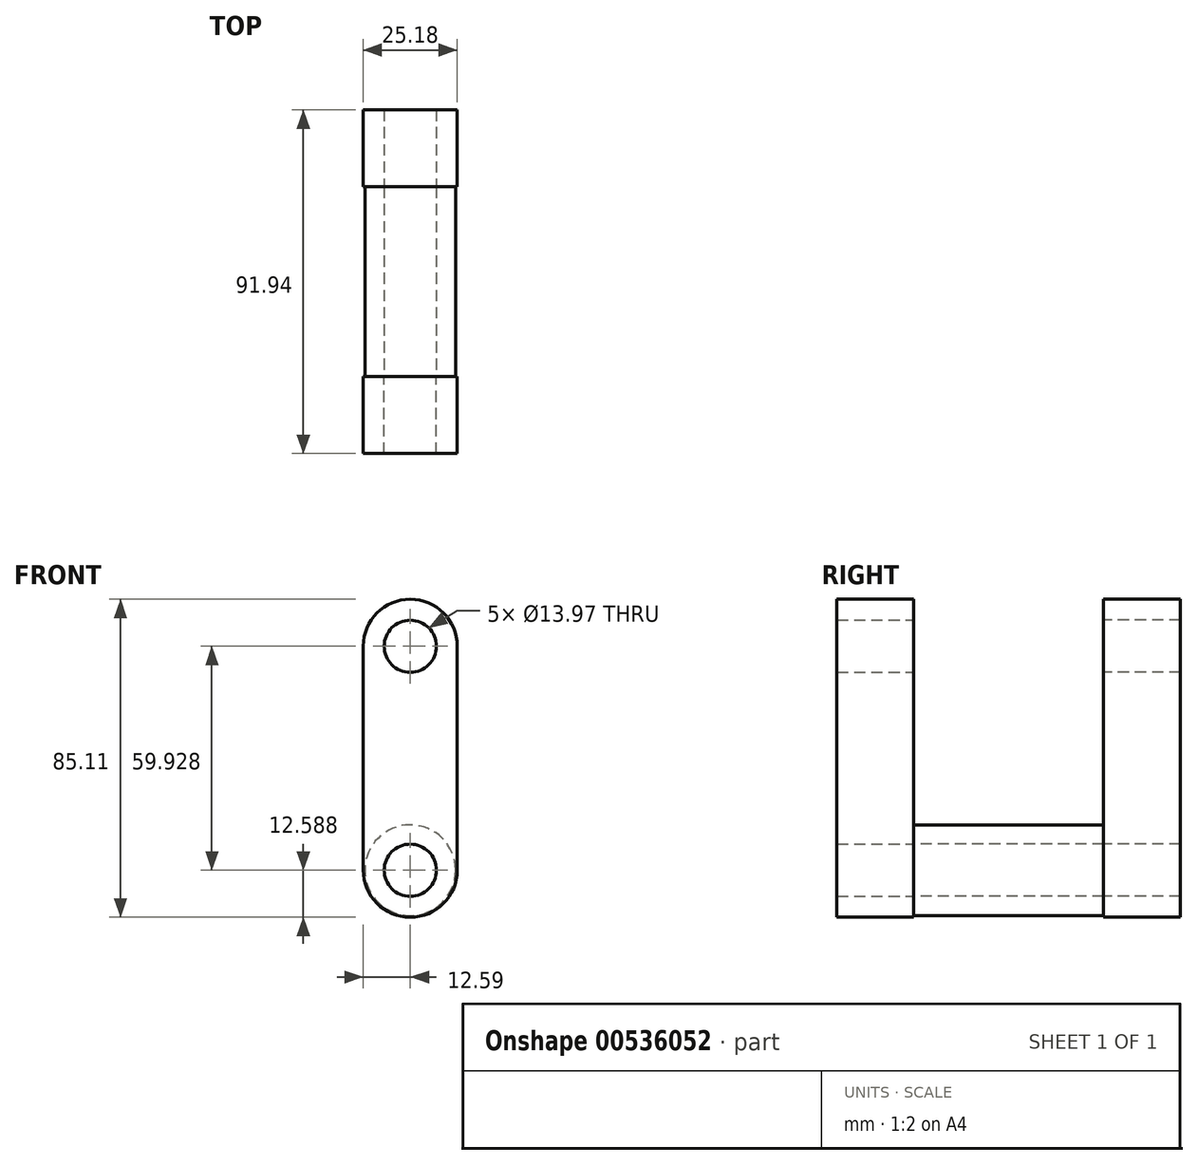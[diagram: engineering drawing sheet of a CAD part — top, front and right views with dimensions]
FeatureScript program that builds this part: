
annotation { "Feature Type Name" : "Feature", "Feature Type Description" : "" }
export const myFeature = defineFeature(function(context is Context, id is Id, definition is map)
    precondition{}
    {
        {
            var Q0;
            Q0=qCreatedBy(makeId("Front.planeOp"),FACE);
            cPlane(context, id + "F0", {"entities" : qUnion([Q0]), "cplaneType" : CPlaneType.OFFSET, "offset" : 25.4 * mm, "width" : 152.4 * mm, "height" : 152.4 * mm});
        }
        {
            var Q0;
            Q0=qCreatedBy(id+"F0.planeOp",FACE);
            var sketch = newSketch(context, id + "F1", { "sketchPlane" : qUnion([Q0])});
            skLineSegment(sketch, "E0.bottom", {"start": v(-12.6, 37.3) * mm, "end": v(12.6, 37.3) * mm});
            skLineSegment(sketch, "E0.top", {"start": v(-12.6, -22.63) * mm, "end": v(12.6, -22.63) * mm});
            skLineSegment(sketch, "E0.left", {"start": v(-12.6, 37.3) * mm, "end": v(-12.6, -22.63) * mm});
            skLineSegment(sketch, "E0.right", {"start": v(12.6, 37.3) * mm, "end": v(12.6, -22.63) * mm});
            skArc(sketch, "E1", {"start": v(12.6, 37.3) * mm, "mid": v(0, 49.89) * mm, "end": v(-12.6, 37.3) * mm});
            skArc(sketch, "E2", {"start": v(-12.6, -22.63) * mm, "mid": v(0, -35.22) * mm, "end": v(12.6, -22.63) * mm});
            skCircle(sketch, "E3", {"center": v(0, 37.3) * mm, "radius": 6.99 * mm});
            skCircle(sketch, "E4", {"center": v(0, -22.63) * mm, "radius": 6.99 * mm});
            skSolve(sketch);
        }
        {
            var Q0;
            Q0 = qSketchRegion(id + "F1", true);
            extrude(context, id + "F2", {"entities" : qUnion([Q0]), "depth" : 20.57 * mm, "offsetDistance" : 25.4 * mm});
        }
        {
            var Q0;
            Q0=makeQuery(id+"F2.opExtrude","SWEPT_BODY",BODY,{"disambiguationData":[OSD([sQuery(id+"F1.wireOp",EDGE,"E0.left"),sQuery(id+"F1.wireOp",EDGE,"E0.right"),sQuery(id+"F1.wireOp",EDGE,"E1"),sQuery(id+"F1.wireOp",EDGE,"E2"),sQuery(id+"F1.wireOp",EDGE,"E3"),sQuery(id+"F1.wireOp",EDGE,"E4")])]});
            var Q1;
            Q1=qCreatedBy(makeId("Front.planeOp"),FACE);
            mirror(context, id + "F3", {"entities" : qUnion([Q0]), "mirrorPlane" : qUnion([Q1])});
        }
        {
            var Q0;
            Q0=makeQuery(id+"F2.opExtrude","CAP_FACE",FACE,{"disambiguationData":[OSD([sQuery(id+"F1.wireOp",EDGE,"E0.left"),sQuery(id+"F1.wireOp",EDGE,"E0.right"),sQuery(id+"F1.wireOp",EDGE,"E1"),sQuery(id+"F1.wireOp",EDGE,"E2"),sQuery(id+"F1.wireOp",EDGE,"E3"),sQuery(id+"F1.wireOp",EDGE,"E4")])],"isStart":true});
            var sketch = newSketch(context, id + "F4", { "sketchPlane" : qUnion([Q0])});
            skCircle(sketch, "E5", {"center": v(0, -22.63) * mm, "radius": 12.14 * mm});
            skSolve(sketch);
        }
        {
            var Q0;
            Q0=makeQuery(id+"F4.imprint","IMPRINT",FACE,{"disambiguationData":[TD([[makeQuery(id+"F4.imprint","IMPRINT",EDGE,{"derivedFrom":sQuery(id+"F4.wireOp",EDGE,"E5")}),1.0]])]});
            extrude(context, id + "F5", {"entities" : qUnion([Q0]), "endBound" : BoundingType.UP_TO_NEXT, "depth" : 25.4 * mm, "offsetDistance" : 25.4 * mm});
        }
    });
